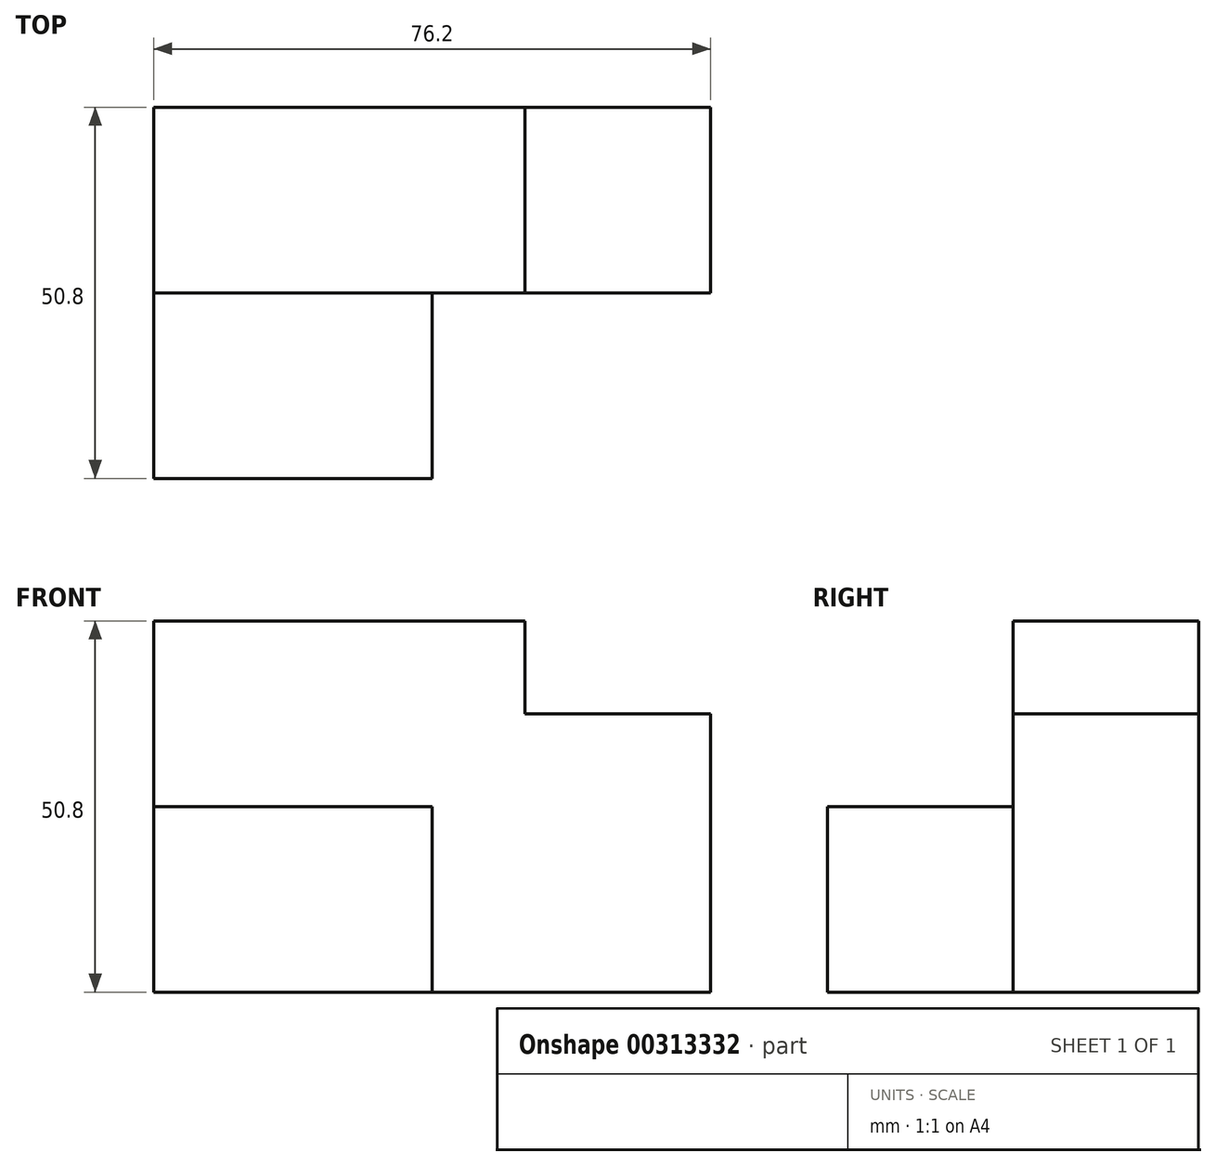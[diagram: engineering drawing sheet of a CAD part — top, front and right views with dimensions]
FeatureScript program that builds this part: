
annotation { "Feature Type Name" : "Feature", "Feature Type Description" : "" }
export const myFeature = defineFeature(function(context is Context, id is Id, definition is map)
    precondition{}
    {
        {
            var Q0;
            Q0=qCreatedBy(makeId("Front.planeOp"),FACE);
            var sketch = newSketch(context, id + "F0", { "sketchPlane" : qUnion([Q0])});
            skLineSegment(sketch, "E0", {"start": v(-42.4, -55.87) * mm, "end": v(33.8, -55.87) * mm});
            skLineSegment(sketch, "E1", {"start": v(33.8, -55.87) * mm, "end": v(33.8, -17.77) * mm});
            skLineSegment(sketch, "E2", {"start": v(33.8, -17.77) * mm, "end": v(8.4, -17.77) * mm});
            skLineSegment(sketch, "E3", {"start": v(8.4, -17.77) * mm, "end": v(8.4, -5.07) * mm});
            skLineSegment(sketch, "E4", {"start": v(8.4, -5.07) * mm, "end": v(-42.4, -5.07) * mm});
            skLineSegment(sketch, "E5", {"start": v(-42.4, -5.07) * mm, "end": v(-42.4, -55.87) * mm});
            skSolve(sketch);
        }
        {
            var Q0;
            Q0 = qSketchRegion(id + "F0", true);
            extrude(context, id + "F1", {"entities" : qUnion([Q0]), "depth" : 25.4 * mm});
        }
        {
            var Q0;
            Q0=makeQuery(id+"F1.opExtrude","CAP_FACE",FACE,{"disambiguationData":[OSD([sQuery(id+"F0.wireOp",EDGE,"E0"),sQuery(id+"F0.wireOp",EDGE,"E1"),sQuery(id+"F0.wireOp",EDGE,"E2"),sQuery(id+"F0.wireOp",EDGE,"E3"),sQuery(id+"F0.wireOp",EDGE,"E4"),sQuery(id+"F0.wireOp",EDGE,"E5")])],"isStart":false});
            var sketch = newSketch(context, id + "F2", { "sketchPlane" : qUnion([Q0])});
            skLineSegment(sketch, "E6", {"start": v(-42.4, -55.87) * mm, "end": v(-42.4, -30.47) * mm});
            skLineSegment(sketch, "E7", {"start": v(-42.4, -30.47) * mm, "end": v(-4.3, -30.47) * mm});
            skLineSegment(sketch, "E8", {"start": v(-4.3, -30.47) * mm, "end": v(-4.3, -55.87) * mm});
            skLineSegment(sketch, "E9", {"start": v(-4.3, -55.87) * mm, "end": v(-42.4, -55.87) * mm});
            skSolve(sketch);
        }
        {
            var Q0;
            Q0=makeQuery(id+"F2.imprint","IMPRINT",FACE,{"disambiguationData":[TD([[makeQuery(id+"F2.imprint","IMPRINT",EDGE,{"derivedFrom":sQuery(id+"F2.wireOp",EDGE,"E6")}),1.0]])]});
            extrude(context, id + "F3", {"entities" : qUnion([Q0]), "operationType" : NewBodyOperationType.ADD, "depth" : 25.4 * mm});
        }
    });
